# Revit family: 1121xxx Mashiko 600 LED
name_source: partatom
category: Lighting Fixtures
revit_build: Autodesk Revit 2018 (Build: 20170223_1515(x64)
units: mm (PartAtom-declared; Revit-internal decimal feet)

## family parameters
Cut with Voids When Loaded = No
Host = Face
Light Source = Yes
OmniClass Number = 23.80.70.00
OmniClass Title = Lighting
Part Type = Normal
Room Calculation Point = No
Round Connector Dimension = Use Diameter
Shared = No

## types (7) — shared parameters
Assembly Code = D5020200
Color Filter = 16777215
Dimmable = No
Dimming Lamp Color Temperature Shift = <None>
Emit Shape Visible in Rendering = No
Emit from Rectangle Length = 60 mm  [stored 0.19685 ft]
IP Rating = IP44
Length = 80 mm  [stored 0.262467 ft]
Light Source From Wall = 40 mm  [stored 0.131234 ft]
Manufacturer = Astro Lighting Ltd, CM20 2DP
Mountable on normally flammable surfaces = Yes
Number of Poles = 1
Product Documentation = http://www.astrolighting.co.uk
Suitable for bathroom zone = Zones 2 and 3
Tilt Angle = 90.00°
URL = www.astrolighting.co.uk
Voltage = 230 V
Width = 80 mm  [stored 0.262467 ft]

## per-type parameters (varying)
| type | 900 Visibility | Apparent Load | Casing Material | Class | Connector Placement | Description | Diffuser Length | Emit from Rectangle Width | Height | Lamp | Lamp included | Luminaire Lamp Efficiency Rating | Model | Photometric Web File | Type Comments | Wattage Comments | Weight |
| 0550 Mashiko 360 | No | 13 VA | Astro - Steel - Chrome Finish | 2 | 275 mm | Wall Light | 330 mm | 330 mm | 360 mm  [stored 1.1811 ft] | 2G11 | No | B | 0550 Mashiko 360 | 0550 MASHIKO 360.ies | Can be mounted horizontally or vertically. Includes internal electronic ballast. | 18w | 1.7kg |
| 7099 Mashiko 360 LED | No | 8 VA | Astro - Steel - Chrome Finish | 2 | 275 mm | Wall Light | 330 mm | 330 mm | 360 mm  [stored 1.1811 ft] | LED | Yes | A | 7099 Mashiko 360 LED | MASHIKO LED 360.ies | Can be mounted horizontally or vertically. Includes integral LED driver. | 7.2w | 1.4kg |
| 0583 Mashiko 500 | No | 33 VA | Astro - Steel - Chrome Finish | 1 | 468 mm | Wall Light | 480 mm | 480 mm | 510 mm | 2G11 | No | B | 0583 Mashiko 500 | 0583 MASHIKO 500.ies | Can be mounted horizontally or vertically. Includes internal electronic ballast. | 36w | 2.3kg |
| 0878 Mashiko 600 | No | 21 VA | Astro - Steel - Chrome Finish | 2 | 107.5 mm | Mirror Light | 580 mm | 580 mm | 610 mm | T5 | No | A-C | 0878 Mashiko 600 | 0878 MASHIKO 600.ies | Can be mounted horizontally or vertically. Includes internal electronic ballast. | 24w | 2.43kg |
| 7134 Mashiko 600 LED | No | 16 VA | Astro - Steel - Chrome Finish | 2 | 107.5 mm | Mirror Light | 580 mm | 580 mm | 610 mm | LED | Yes | A | 7134 Mashiko 600 LED | 7134MASHIKO LED 600.ies | Can be mounted horizontally or vertically. Includes integral LED driver. | 10.8w | 2.09kg |
| 0911 Mashiko 900 | Yes | 38 VA | Astro - Steel - Chrome Finish | 2 | 200 mm  [stored 0.656168 ft] | Mirror Light | 435 mm  [stored 1.42717 ft] | 880 mm  [stored 2.88714 ft] | 910 mm | T5 | No | A-C | 0911 Mashiko 900 | 0911 MASHIKO 900.ies | Includes integral electronic ballast. Can be mounted horizontally or vertically. | 39w | 3.46kg |
| 7043 Mashiko 360 (Silver) | No | 13 VA | Astro - Steel - Silver Paint | 2 | 275 mm | Wall Light | 330 mm | 330 mm | 360 mm  [stored 1.1811 ft] | 2G11 | No | B | 7043 Mashiko 360 Silver | 0550 MASHIKO 360.ies | Can be mounted horizontally or vertically. Includes internal electronic ballast. | 18w | 1.7kg |

note: [stored X ft] marks values corroborated as IEEE doubles in the binary element streams (Revit-internal decimal feet)

## geometry (parser evidence)
native form markers: Sweep x3
no freeform markers — native parametric forms only
